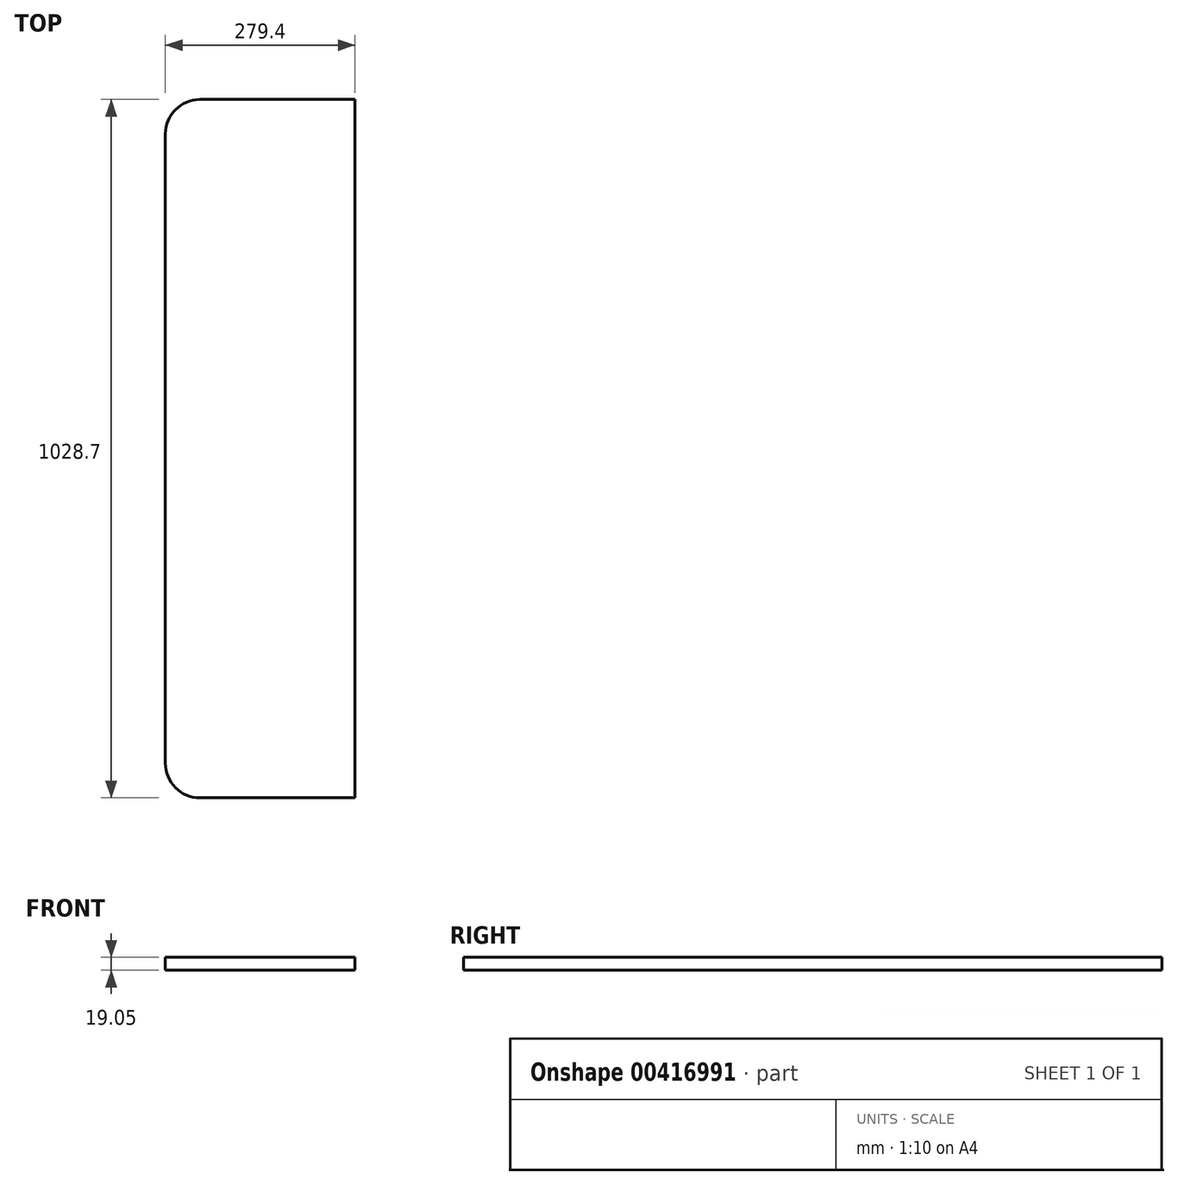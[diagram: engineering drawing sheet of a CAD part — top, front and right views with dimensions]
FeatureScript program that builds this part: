
annotation { "Feature Type Name" : "Feature", "Feature Type Description" : "" }
export const myFeature = defineFeature(function(context is Context, id is Id, definition is map)
    precondition{}
    {
        {
            var Q0;
            Q0=qCreatedBy(makeId("Top.planeOp"),FACE);
            var sketch = newSketch(context, id + "F0", { "sketchPlane" : qUnion([Q0])});
            skLineSegment(sketch, "E0.bottom", {"start": v(-102.11, 708.27) * mm, "end": v(126.49, 708.27) * mm});
            skLineSegment(sketch, "E0.top", {"start": v(-102.11, -320.43) * mm, "end": v(126.49, -320.43) * mm});
            skLineSegment(sketch, "E0.left", {"start": v(-152.91, 657.47) * mm, "end": v(-152.91, -269.63) * mm});
            skLineSegment(sketch, "E0.right", {"start": v(126.49, 708.27) * mm, "end": v(126.49, -320.43) * mm});
            skPoint(sketch, "E1.visualSharp", {"position": v(-152.91, 708.27) * mm});
            skArc(sketch, "E1.filletArc", {"start": v(-102.11, 708.27) * mm, "mid": v(-138.04, 693.4) * mm, "end": v(-152.91, 657.47) * mm});
            skPoint(sketch, "E2.visualSharp", {"position": v(-152.91, -320.43) * mm});
            skArc(sketch, "E2.filletArc", {"start": v(-152.91, -269.63) * mm, "mid": v(-138.04, -305.55) * mm, "end": v(-102.11, -320.43) * mm});
            skSolve(sketch);
        }
        {
            var Q0;
            Q0 = qSketchRegion(id + "F0", true);
            extrude(context, id + "F1", {"entities" : qUnion([Q0]), "depth" : 19.05 * mm});
        }
    });
